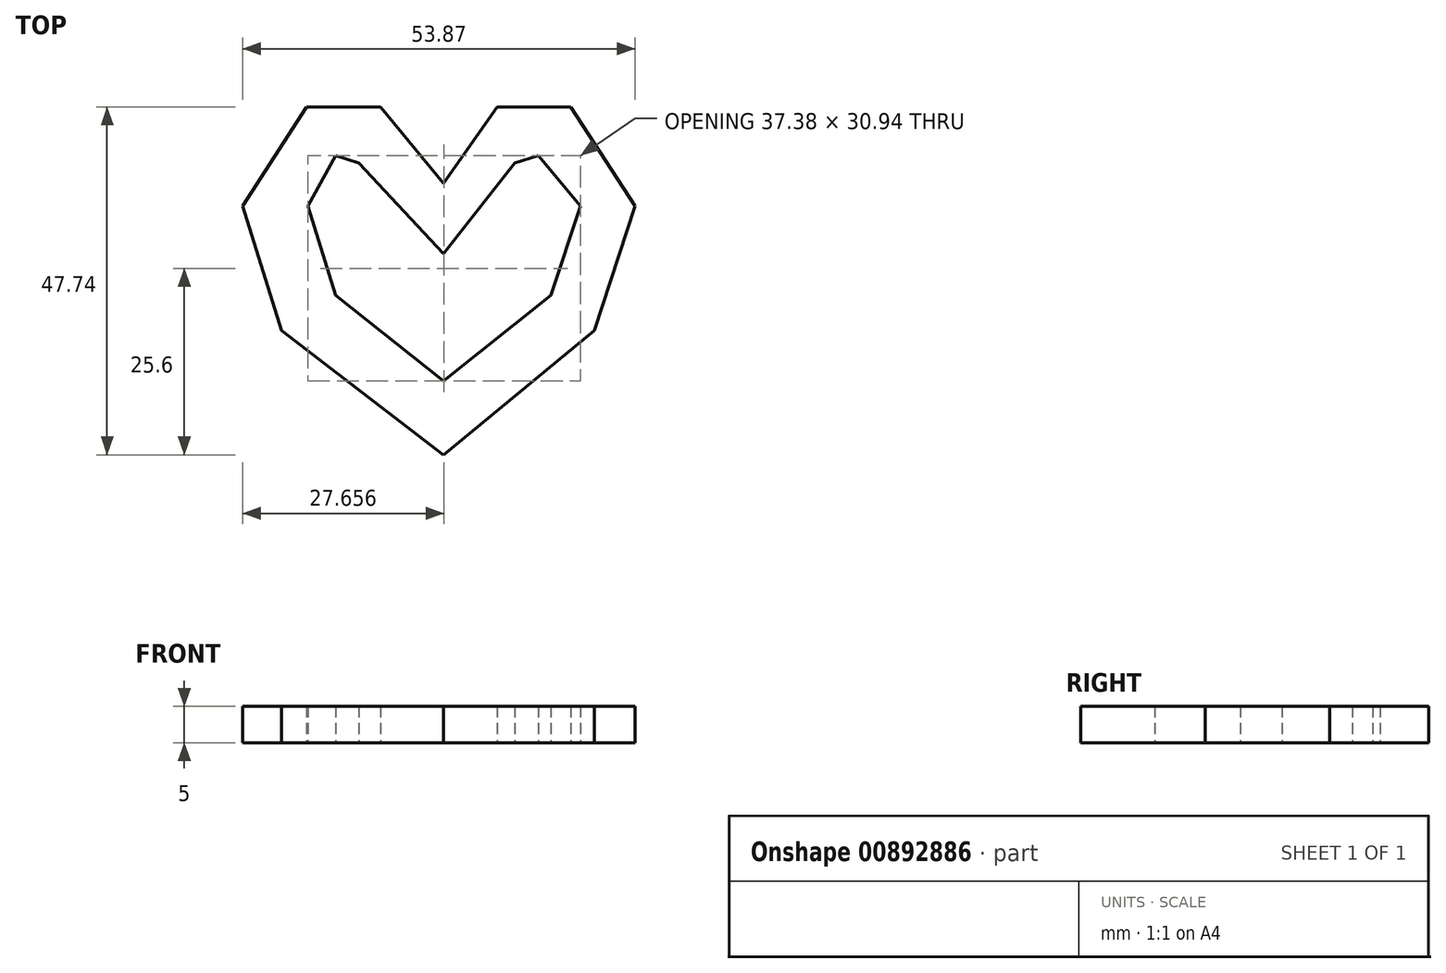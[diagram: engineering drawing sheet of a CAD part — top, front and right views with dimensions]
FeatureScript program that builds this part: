
annotation { "Feature Type Name" : "Feature", "Feature Type Description" : "" }
export const myFeature = defineFeature(function(context is Context, id is Id, definition is map)
    precondition{}
    {
        {
            var Q0;
            Q0=qCreatedBy(makeId("Top.planeOp"),FACE);
            var sketch = newSketch(context, id + "F0", { "sketchPlane" : qUnion([Q0])});
            skLineSegment(sketch, "E0", {"start": v(0, -27.6) * mm, "end": v(20.67, -10.53) * mm});
            skLineSegment(sketch, "E1", {"start": v(0, -27.6) * mm, "end": v(-22.27, -10.53) * mm});
            skLineSegment(sketch, "E2", {"start": v(-22.27, -10.53) * mm, "end": v(-27.6, 6.53) * mm});
            skLineSegment(sketch, "E3", {"start": v(20.67, -10.53) * mm, "end": v(26.27, 6.53) * mm});
            skLineSegment(sketch, "E4", {"start": v(-27.6, 6.53) * mm, "end": v(-18.8, 20.14) * mm});
            skLineSegment(sketch, "E5", {"start": v(26.27, 6.53) * mm, "end": v(17.47, 20.14) * mm});
            skLineSegment(sketch, "E6", {"start": v(-18.8, 20.14) * mm, "end": v(-8.67, 20.14) * mm});
            skLineSegment(sketch, "E7", {"start": v(17.47, 20.14) * mm, "end": v(7.33, 20.14) * mm});
            skLineSegment(sketch, "E8", {"start": v(-8.67, 20.14) * mm, "end": v(0, 9.64) * mm});
            skLineSegment(sketch, "E9", {"start": v(7.33, 20.14) * mm, "end": v(0, 9.64) * mm});
            skLineSegment(sketch, "E10", {"start": v(0, -17.47) * mm, "end": v(-14.8, -5.73) * mm});
            skLineSegment(sketch, "E11", {"start": v(-14.8, -5.73) * mm, "end": v(-18.64, 6.53) * mm});
            skLineSegment(sketch, "E12", {"start": v(-18.64, 6.53) * mm, "end": v(-14.8, 13.47) * mm});
            skLineSegment(sketch, "E13", {"start": v(-14.8, 13.47) * mm, "end": v(-11.67, 12.44) * mm});
            skLineSegment(sketch, "E14", {"start": v(-11.67, 12.44) * mm, "end": v(0, 0) * mm});
            skLineSegment(sketch, "E15", {"start": v(0, 0) * mm, "end": v(9.73, 12.44) * mm});
            skLineSegment(sketch, "E16", {"start": v(9.73, 12.44) * mm, "end": v(13.02, 13.47) * mm});
            skLineSegment(sketch, "E17", {"start": v(13.02, 13.47) * mm, "end": v(18.75, 6.53) * mm});
            skLineSegment(sketch, "E18", {"start": v(18.75, 6.53) * mm, "end": v(14.72, -5.73) * mm});
            skLineSegment(sketch, "E19", {"start": v(14.72, -5.73) * mm, "end": v(0, -17.47) * mm});
            skSolve(sketch);
        }
        {
            var Q0;
            Q0=makeQuery(id+"F0.imprint","IMPRINT",FACE,{"disambiguationData":[TD([[makeQuery(id+"F0.imprint","IMPRINT",EDGE,{"derivedFrom":sQuery(id+"F0.wireOp",EDGE,"E0")}),1.0]])]});
            extrude(context, id + "F1", {"entities" : qUnion([Q0]), "depth" : 5 * mm, "offsetDistance" : 25.4 * mm});
        }
    });
